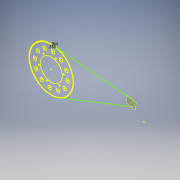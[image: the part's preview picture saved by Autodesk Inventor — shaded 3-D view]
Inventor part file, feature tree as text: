
AUTODESK INVENTOR PART (.ipt)
format: ipt  version: 2019.3 (Build 233278000, 278)  size: 177,152 bytes
history: native  units: in
note: dims shown in document units (in); Inventor stores cm internally (conversion verified against a paired STEP export)
features: other x5, plane x2, sweep x1, reference x1, sketch x1
ambient origin geometry x8: Origin, YZ Plane, XZ Plane, XY Plane, X Axis, Y Axis, Z Axis, Center Point
bodies: Body1 (feature_tree)
feature tree (10):
  plane  "Work Plane1"
  plane  "Work Plane2"
  sweep  "Sweep1"
  reference  "Reference2"
  sketch  "Sketch2"  dims[d2=0.3937in d3=0.2362in d4=0.0in d5=0.0in]
  other  "<userpath>\Desktop\3dprojects\OpenEmoto\Swingarm3\Swingarm3.iam"
  other  "Swingarm3.iam"
  other  "Sprocket92T:1"
  other  "Denzel4500Motor:1"
  other  "DriveSprocket12T:1"
